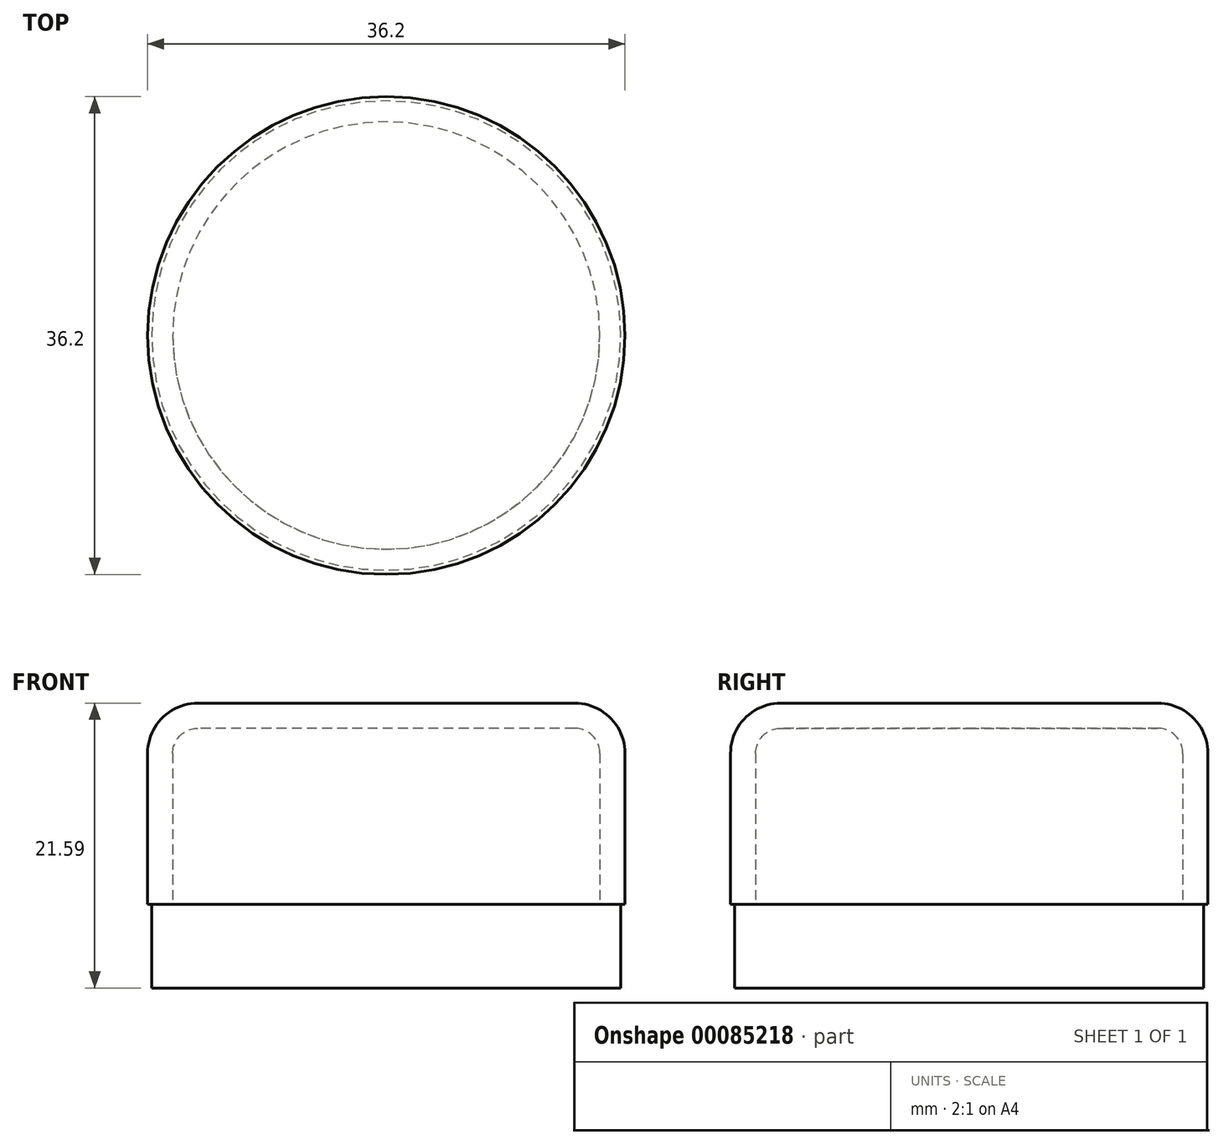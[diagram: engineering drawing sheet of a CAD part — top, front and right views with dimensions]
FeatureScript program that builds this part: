
annotation { "Feature Type Name" : "Feature", "Feature Type Description" : "" }
export const myFeature = defineFeature(function(context is Context, id is Id, definition is map)
    precondition{}
    {
        {
            var Q0;
            Q0=qCreatedBy(makeId("Top.planeOp"),FACE);
            cPlane(context, id + "F0", {"entities" : qUnion([Q0]), "cplaneType" : CPlaneType.OFFSET, "offset" : 6.35 * mm, "width" : 152.4 * mm, "height" : 152.4 * mm});
        }
        {
            var Q0;
            Q0=qCreatedBy(id+"F0.planeOp",FACE);
            var sketch = newSketch(context, id + "F1", { "sketchPlane" : qUnion([Q0])});
            skCircle(sketch, "E0", {"center": v(0, 0) * mm, "radius": 18.1 * mm});
            skSolve(sketch);
        }
        {
            var Q0;
            Q0=makeQuery(id+"F1.imprint","IMPRINT",FACE,{"disambiguationData":[TD([[makeQuery(id+"F1.imprint","IMPRINT",EDGE,{"derivedFrom":sQuery(id+"F1.wireOp",EDGE,"E0")}),1.0]])]});
            extrude(context, id + "F2", {"entities" : qUnion([Q0]), "depth" : 15.24 * mm});
        }
        {
            var Q0;
            Q0=makeQuery(id+"F2.opExtrude","CAP_EDGE",EDGE,{"disambiguationData":[OSD([sQuery(id+"F1.wireOp",EDGE,"E0")])],"isStart":false});
            fillet(context, id + "F3", {"entities" : qUnion([Q0]), "radius" : 3.8 * mm, "tangentPropagation" : true, "allowEdgeOverflow" : false});
        }
        {
            var Q0;
            Q0=qCreatedBy(makeId("Top.planeOp"),FACE);
            var sketch = newSketch(context, id + "F4", { "sketchPlane" : qUnion([Q0])});
            skCircle(sketch, "E1", {"center": v(0, 0) * mm, "radius": 17.78 * mm});
            skSolve(sketch);
        }
        {
            var Q0;
            Q0=makeQuery(id+"F2.opExtrude","CAP_FACE",FACE,{"disambiguationData":[OSD([sQuery(id+"F1.wireOp",EDGE,"E0")])],"isStart":true});
            shell(context, id + "F5", {"entities" : qUnion([Q0]), "thickness" : 1.9 * mm});
        }
        {
            var Q0;
            Q0 = qSketchRegion(id + "F4", true);
            extrude(context, id + "F6", {"entities" : qUnion([Q0]), "operationType" : NewBodyOperationType.ADD, "depth" : 6.35 * mm});
        }
    });
